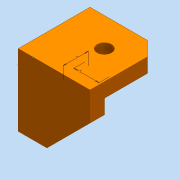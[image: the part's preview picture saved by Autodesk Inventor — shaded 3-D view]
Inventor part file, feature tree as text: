
AUTODESK INVENTOR PART (.ipt)
format: ipt  version: 2016 (Build 200138000, 138)  size: 125,440 bytes
history: native  units: mm
features: sketch x4, chamfer x3, extrude x2, hole x2
ambient origin geometry x8: Origin, YZ Plane, XZ Plane, XY Plane, X Axis, Y Axis, Z Axis, Center Point
bodies: Solid1 (feature_tree)
feature tree (11):
  extrude  "Extrusion1"  Depth=20.0mm
  extrude  "Extrusion2"  Depth=16.0mm TaperAngle=0.0deg
  hole  "Hole2"  [1 undecoded]
  hole  "Hole3"  [1 undecoded]
  chamfer  "Chamfer1"  Distance=4.0mm Angle=45.0deg
  chamfer  "Chamfer2"  Distance=7.0mm
  chamfer  "Chamfer3"  Distance=7.0mm
  sketch  "Sketch3"  dims[d15=8.0mm d16=8.0mm d17=4.0mm d18=6.0mm d19=8.0mm d20=2.0mm d21=90.0deg d22=8.0mm d23=20.594885mm]
  sketch  "Sketch4"  dims[d24=8.0mm d25=8.0mm d26=4.0mm d27=6.0mm d28=8.0mm d29=2.0mm d30=90.0deg d31=8.0mm d32=20.594885mm d42=12.0mm d43=2.0mm d44=45.0deg d45=4.0mm d46=2.0mm d47=45.0deg d48=4.0mm d49=2.0mm d50=45.0deg d51=7.0mm d52=7.0mm]
  sketch  "Sketch1"  dims[d0=20.0mm d1=20.0mm]
  sketch  "Sketch2"  dims[d2=4.0mm d3=0.0mm d4=16.0mm d5=0.0mm]
note: 2 required parameter values undecoded (feature->parameter linkage not recoverable at this tier; creation-order binding heuristic only, values carry confidence <= 0.55)
